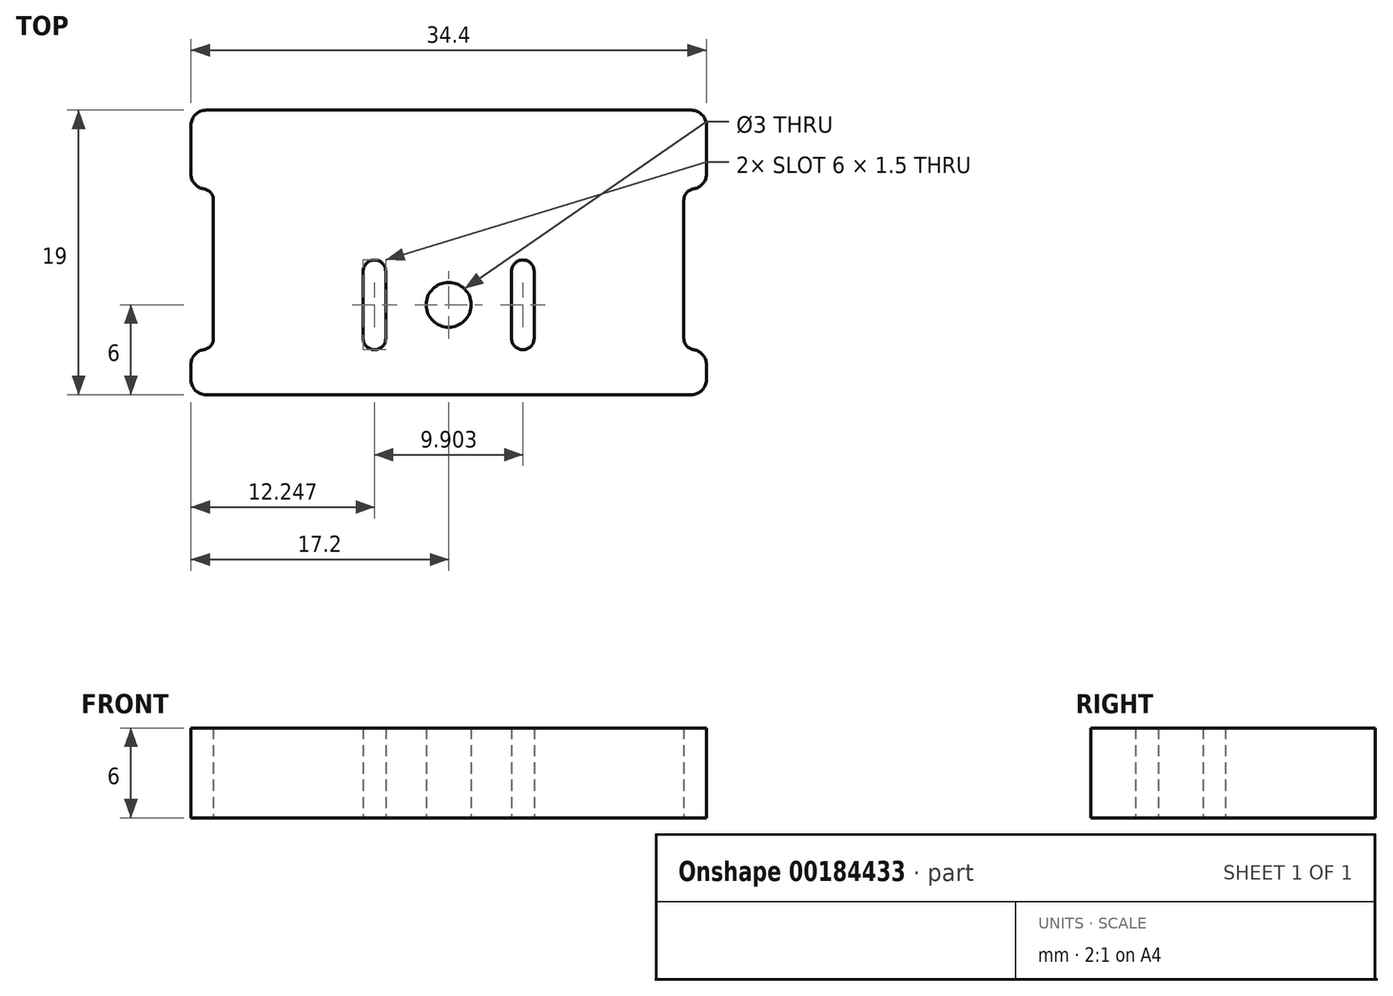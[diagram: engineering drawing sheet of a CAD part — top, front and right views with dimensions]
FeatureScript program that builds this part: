
annotation { "Feature Type Name" : "Feature", "Feature Type Description" : "" }
export const myFeature = defineFeature(function(context is Context, id is Id, definition is map)
    precondition{}
    {
        {
            var Q0;
            Q0=qCreatedBy(makeId("Top.planeOp"),FACE);
            var sketch = newSketch(context, id + "F0", { "sketchPlane" : qUnion([Q0])});
            skLineSegment(sketch, "E0.bottom", {"start": v(-17.2, 11) * mm, "end": v(17.2, 11) * mm});
            skLineSegment(sketch, "E0.top", {"start": v(-17.2, -8) * mm, "end": v(17.2, -8) * mm});
            skLineSegment(sketch, "E0.left", {"start": v(-17.2, 11) * mm, "end": v(-17.2, -8) * mm});
            skLineSegment(sketch, "E0.right", {"start": v(17.2, 11) * mm, "end": v(17.2, -8) * mm});
            skLineSegment(sketch, "E1", {"start": v(0, 11) * mm, "end": v(0, -8) * mm, "construction": true});
            skLineSegment(sketch, "E2", {"start": v(4.95, 0.25) * mm, "end": v(4.95, -4.25) * mm});
            skArc(sketch, "E3.0.startCap", {"start": v(4.2, 0.25) * mm, "mid": v(4.95, 1) * mm, "end": v(5.7, 0.25) * mm});
            skArc(sketch, "E3.0.endCap", {"start": v(5.7, -4.25) * mm, "mid": v(4.95, -5) * mm, "end": v(4.2, -4.25) * mm});
            skLineSegment(sketch, "E3.0.left", {"start": v(5.7, 0.25) * mm, "end": v(5.7, -4.25) * mm});
            skLineSegment(sketch, "E3.0.right", {"start": v(4.2, 0.25) * mm, "end": v(4.2, -4.25) * mm});
            skLineSegment(sketch, "E4", {"start": v(-4.95, 0.25) * mm, "end": v(-4.95, -4.25) * mm});
            skArc(sketch, "E5.0.startCap", {"start": v(-5.7, 0.25) * mm, "mid": v(-4.95, 1) * mm, "end": v(-4.2, 0.25) * mm});
            skArc(sketch, "E5.0.endCap", {"start": v(-4.2, -4.25) * mm, "mid": v(-4.95, -5) * mm, "end": v(-5.7, -4.25) * mm});
            skLineSegment(sketch, "E5.0.left", {"start": v(-4.2, 0.25) * mm, "end": v(-4.2, -4.25) * mm});
            skLineSegment(sketch, "E5.0.right", {"start": v(-5.7, 0.25) * mm, "end": v(-5.7, -4.25) * mm});
            skPoint(sketch, "E6", {"position": v(-4.95, -2) * mm});
            skPoint(sketch, "E7", {"position": v(4.95, -2) * mm});
            skLineSegment(sketch, "E8", {"start": v(-16.45, 5) * mm, "end": v(-16.45, -4.25) * mm});
            skArc(sketch, "E9.0.startCap", {"start": v(-17.2, 5) * mm, "mid": v(-16.45, 5.75) * mm, "end": v(-15.7, 5) * mm});
            skArc(sketch, "E9.0.endCap", {"start": v(-15.7, -4.25) * mm, "mid": v(-16.45, -5) * mm, "end": v(-17.2, -4.25) * mm});
            skLineSegment(sketch, "E9.0.left", {"start": v(-15.7, 5) * mm, "end": v(-15.7, -4.25) * mm});
            skLineSegment(sketch, "E9.0.right", {"start": v(-17.2, 5) * mm, "end": v(-17.2, -4.25) * mm});
            skPoint(sketch, "E10", {"position": v(-16.45, 0.37) * mm});
            skLineSegment(sketch, "E11", {"start": v(16.45, 5) * mm, "end": v(16.45, -4.25) * mm});
            skArc(sketch, "E12.0.startCap", {"start": v(15.7, 5) * mm, "mid": v(16.45, 5.75) * mm, "end": v(17.2, 5) * mm});
            skArc(sketch, "E12.0.endCap", {"start": v(17.2, -4.25) * mm, "mid": v(16.45, -5) * mm, "end": v(15.7, -4.25) * mm});
            skLineSegment(sketch, "E12.0.left", {"start": v(17.2, 5) * mm, "end": v(17.2, -4.25) * mm});
            skLineSegment(sketch, "E12.0.right", {"start": v(15.7, 5) * mm, "end": v(15.7, -4.25) * mm});
            skPoint(sketch, "E13", {"position": v(16.45, 0.38) * mm});
            skCircle(sketch, "E14", {"center": v(0, -2) * mm, "radius": 1.5 * mm});
            skLineSegment(sketch, "E15", {"start": v(0, 5) * mm, "end": v(-17.2, 5) * mm, "construction": true});
            skSolve(sketch);
        }
        {
            var Q0;
            Q0=makeQuery(id+"F0.imprint","IMPRINT",FACE,{"disambiguationData":[TD([[makeQuery(id+"F0.imprint","IMPRINT",EDGE,{"derivedFrom":sQuery(id+"F0.wireOp",EDGE,"E0.bottom")}),-1.0]])]});
            extrude(context, id + "F1", {"entities" : qUnion([Q0]), "depth" : 6 * mm});
        }
        {
            var Q0;
            Q0=makeQuery(id+"F1.opExtrude","SWEPT_EDGE",EDGE,{"disambiguationData":[OSD([sQuery(id+"F0.wireOp",EDGE,"E0.bottom"),sQuery(id+"F0.wireOp",EDGE,"E0.right")])]});
            var Q1;
            Q1=makeQuery(id+"F1.opExtrude","SWEPT_EDGE",EDGE,{"disambiguationData":[OSD([sQuery(id+"F0.wireOp",EDGE,"E0.top"),sQuery(id+"F0.wireOp",EDGE,"E0.right")])]});
            var Q2;
            Q2=makeQuery(id+"F1.opExtrude","SWEPT_EDGE",EDGE,{"disambiguationData":[OSD([sQuery(id+"F0.wireOp",EDGE,"E0.top"),sQuery(id+"F0.wireOp",EDGE,"E0.left")])]});
            var Q3;
            Q3=makeQuery(id+"F1.opExtrude","SWEPT_EDGE",EDGE,{"disambiguationData":[OSD([sQuery(id+"F0.wireOp",EDGE,"E0.bottom"),sQuery(id+"F0.wireOp",EDGE,"E0.left")])]});
            fillet(context, id + "F2", {"entities" : qUnion([Q0, Q1, Q2, Q3]), "radius" : 1 * mm, "tangentPropagation" : true, "allowEdgeOverflow" : false});
        }
        {
            var Q0;
            Q0=makeQuery(id+"F1.opExtrude","SWEPT_EDGE",EDGE,{"disambiguationData":[OSD([sQuery(id+"F0.wireOp",EDGE,"E0.right"),sQuery(id+"F0.wireOp",EDGE,"E12.0.startCap"),sQuery(id+"F0.wireOp",EDGE,"E12.0.left")])]});
            var Q1;
            Q1=makeQuery(id+"F1.opExtrude","SWEPT_EDGE",EDGE,{"disambiguationData":[OSD([sQuery(id+"F0.wireOp",EDGE,"E0.right"),sQuery(id+"F0.wireOp",EDGE,"E12.0.endCap"),sQuery(id+"F0.wireOp",EDGE,"E12.0.left")])]});
            var Q2;
            Q2=makeQuery(id+"F1.opExtrude","SWEPT_EDGE",EDGE,{"disambiguationData":[OSD([sQuery(id+"F0.wireOp",EDGE,"E0.left"),sQuery(id+"F0.wireOp",EDGE,"E9.0.startCap"),sQuery(id+"F0.wireOp",EDGE,"E9.0.right")])]});
            var Q3;
            Q3=makeQuery(id+"F1.opExtrude","SWEPT_EDGE",EDGE,{"disambiguationData":[OSD([sQuery(id+"F0.wireOp",EDGE,"E0.left"),sQuery(id+"F0.wireOp",EDGE,"E9.0.endCap"),sQuery(id+"F0.wireOp",EDGE,"E9.0.right")])]});
            fillet(context, id + "F3", {"entities" : qUnion([Q0, Q1, Q2, Q3]), "radius" : 1 * mm, "tangentPropagation" : true, "allowEdgeOverflow" : false});
        }
    });
